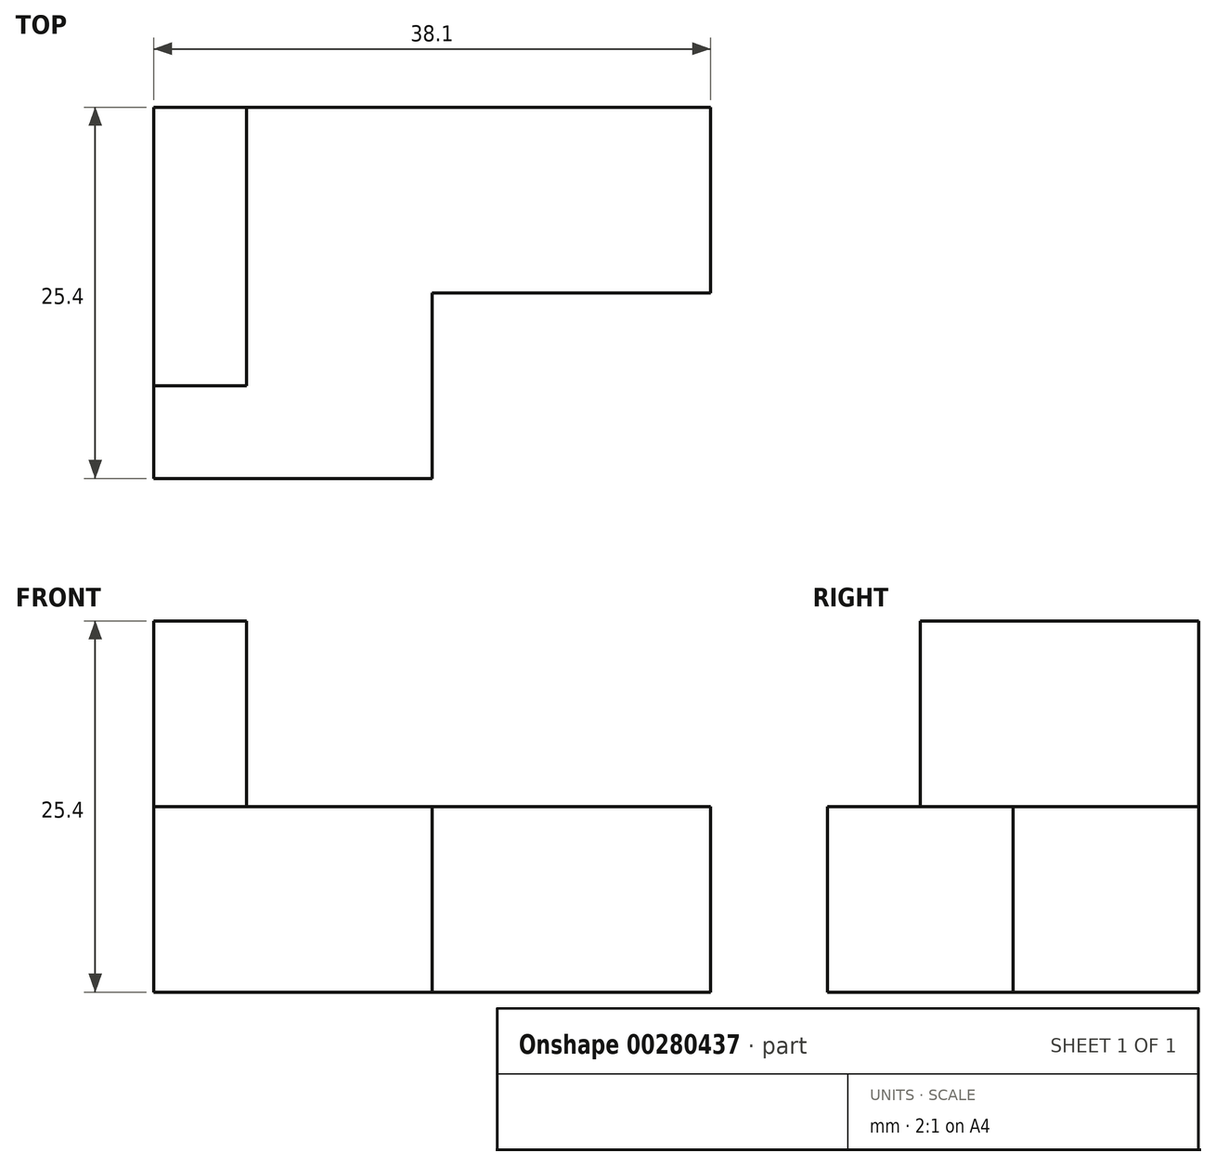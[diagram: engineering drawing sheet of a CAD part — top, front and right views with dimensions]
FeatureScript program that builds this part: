
annotation { "Feature Type Name" : "Feature", "Feature Type Description" : "" }
export const myFeature = defineFeature(function(context is Context, id is Id, definition is map)
    precondition{}
    {
        {
            var Q0;
            Q0=qCreatedBy(makeId("Front.planeOp"),FACE);
            var sketch = newSketch(context, id + "F0", { "sketchPlane" : qUnion([Q0])});
            skLineSegment(sketch, "E0.bottom", {"start": v(0, 25.4) * mm, "end": v(38.1, 25.4) * mm});
            skLineSegment(sketch, "E0.top", {"start": v(0, 0) * mm, "end": v(38.1, 0) * mm});
            skLineSegment(sketch, "E0.left", {"start": v(0, 25.4) * mm, "end": v(0, 0) * mm});
            skLineSegment(sketch, "E0.right", {"start": v(38.1, 25.4) * mm, "end": v(38.1, 0) * mm});
            skSolve(sketch);
        }
        {
            var Q0;
            Q0=makeQuery(id+"F0.imprint","IMPRINT",FACE,{"disambiguationData":[TD([[makeQuery(id+"F0.imprint","IMPRINT",EDGE,{"derivedFrom":sQuery(id+"F0.wireOp",EDGE,"E0.bottom")}),-1.0]])]});
            extrude(context, id + "F1", {"entities" : qUnion([Q0]), "depth" : 25.4 * mm});
        }
        {
            var Q0;
            Q0=qCreatedBy(makeId("Front.planeOp"),FACE);
            var sketch = newSketch(context, id + "F2", { "sketchPlane" : qUnion([Q0])});
            skLineSegment(sketch, "E1.bottom", {"start": v(6.35, 25.4) * mm, "end": v(38.1, 25.4) * mm});
            skLineSegment(sketch, "E1.top", {"start": v(6.35, 12.7) * mm, "end": v(38.1, 12.7) * mm});
            skLineSegment(sketch, "E1.left", {"start": v(6.35, 25.4) * mm, "end": v(6.35, 12.7) * mm});
            skLineSegment(sketch, "E1.right", {"start": v(38.1, 25.4) * mm, "end": v(38.1, 12.7) * mm});
            skSolve(sketch);
        }
        {
            var Q0;
            Q0 = qSketchRegion(id + "F2", true);
            extrude(context, id + "F3", {"entities" : qUnion([Q0]), "operationType" : NewBodyOperationType.REMOVE, "depth" : 25.4 * mm});
        }
        {
            var Q0;
            Q0=qCreatedBy(makeId("Right.planeOp"),FACE);
            var sketch = newSketch(context, id + "F4", { "sketchPlane" : qUnion([Q0])});
            skLineSegment(sketch, "E2.bottom", {"start": v(-25.4, 25.4) * mm, "end": v(-19.05, 25.4) * mm});
            skLineSegment(sketch, "E2.top", {"start": v(-25.4, 12.7) * mm, "end": v(-19.05, 12.7) * mm});
            skLineSegment(sketch, "E2.left", {"start": v(-25.4, 25.4) * mm, "end": v(-25.4, 12.7) * mm});
            skLineSegment(sketch, "E2.right", {"start": v(-19.05, 25.4) * mm, "end": v(-19.05, 12.7) * mm});
            skSolve(sketch);
        }
        {
            var Q0;
            Q0 = qSketchRegion(id + "F4", true);
            extrude(context, id + "F5", {"entities" : qUnion([Q0]), "operationType" : NewBodyOperationType.REMOVE, "depth" : 6.35 * mm});
        }
        {
            var Q0;
            Q0=qCreatedBy(makeId("Top.planeOp"),FACE);
            var sketch = newSketch(context, id + "F6", { "sketchPlane" : qUnion([Q0])});
            skLineSegment(sketch, "E3.bottom", {"start": v(19.05, -25.4) * mm, "end": v(38.1, -25.4) * mm});
            skLineSegment(sketch, "E3.top", {"start": v(19.05, -12.7) * mm, "end": v(38.1, -12.7) * mm});
            skLineSegment(sketch, "E3.left", {"start": v(19.05, -25.4) * mm, "end": v(19.05, -12.7) * mm});
            skLineSegment(sketch, "E3.right", {"start": v(38.1, -25.4) * mm, "end": v(38.1, -12.7) * mm});
            skSolve(sketch);
        }
        {
            var Q0;
            Q0 = qSketchRegion(id + "F6", true);
            extrude(context, id + "F7", {"entities" : qUnion([Q0]), "operationType" : NewBodyOperationType.REMOVE, "depth" : 12.7 * mm});
        }
    });
